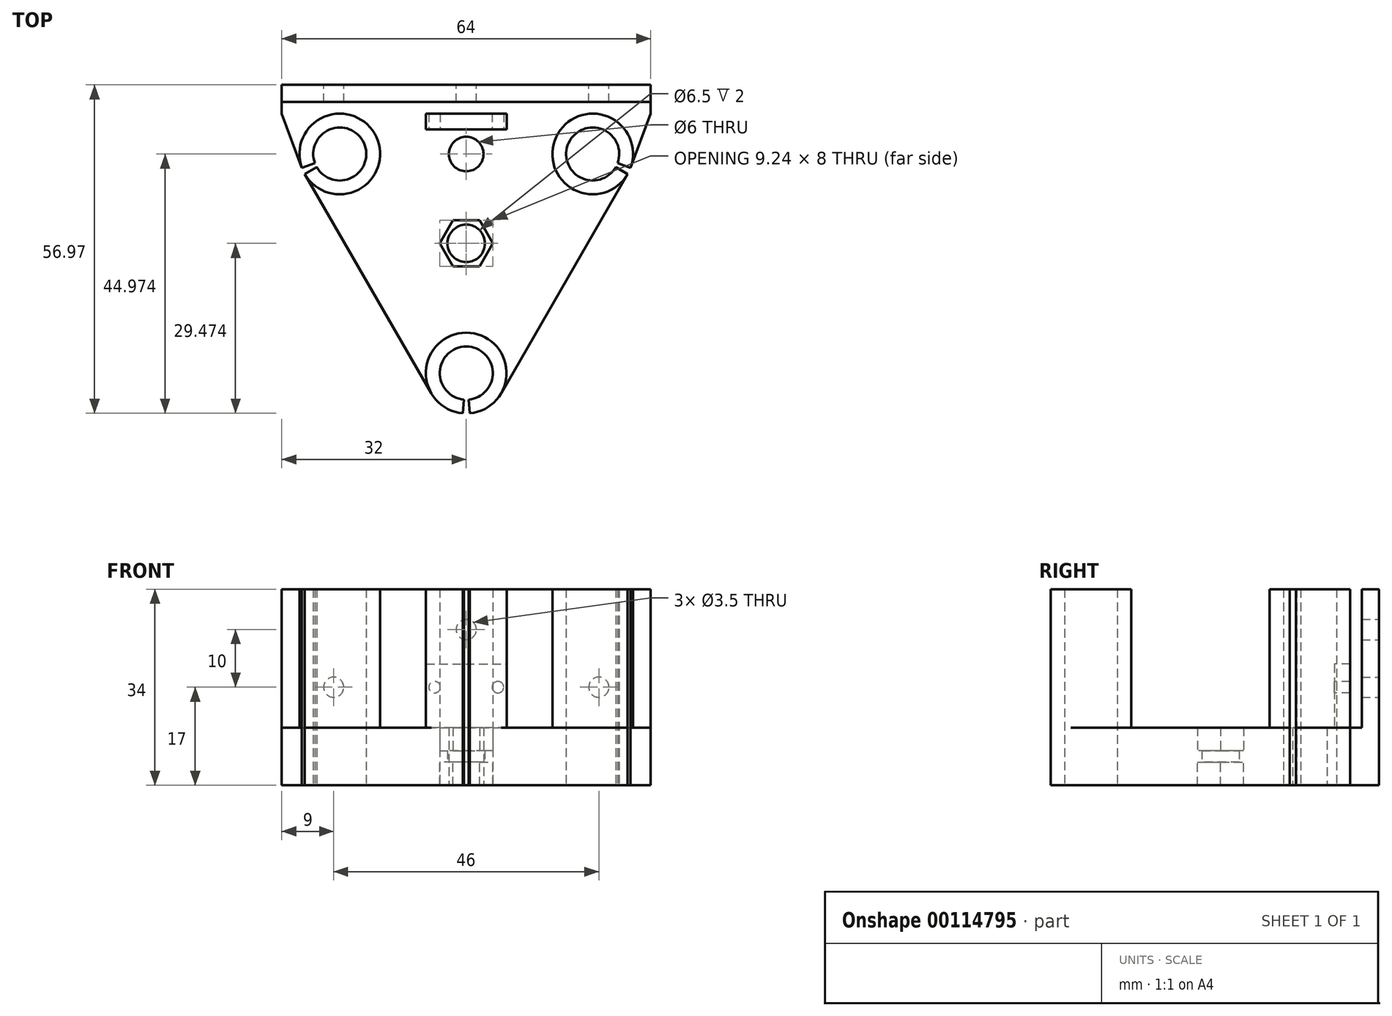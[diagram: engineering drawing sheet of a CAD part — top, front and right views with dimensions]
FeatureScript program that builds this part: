
annotation { "Feature Type Name" : "Feature", "Feature Type Description" : "" }
export const myFeature = defineFeature(function(context is Context, id is Id, definition is map)
    precondition{}
    {
        {
            var Q0;
            Q0=qCreatedBy(makeId("Top.planeOp"),FACE);
            var sketch = newSketch(context, id + "F0", { "sketchPlane" : qUnion([Q0])});
            skLineSegment(sketch, "E0", {"start": v(0, -40.44) * mm, "end": v(0, -2.44) * mm});
            skLineSegment(sketch, "E1", {"start": v(0, -40.44) * mm, "end": v(-21.94, -2.44) * mm});
            skCircle(sketch, "E2", {"center": v(-21.94, -2.44) * mm, "radius": 4.6 * mm});
            skCircle(sketch, "E3", {"center": v(-21.94, -2.44) * mm, "radius": 7 * mm});
            skCircle(sketch, "E4", {"center": v(0, -40.44) * mm, "radius": 7 * mm});
            skCircle(sketch, "E5", {"center": v(0, -40.44) * mm, "radius": 4.6 * mm});
            skLineSegment(sketch, "E6", {"start": v(0, -2.44) * mm, "end": v(0, -33.44) * mm});
            skPoint(sketch, "E7", {"position": v(0, -17.94) * mm});
            skLineSegment(sketch, "E8", {"start": v(0, -40.44) * mm, "end": v(-6.06, -43.94) * mm});
            skLineSegment(sketch, "E9", {"start": v(-21.94, -2.44) * mm, "end": v(-28, -5.94) * mm});
            skLineSegment(sketch, "E10.left", {"start": v(0, -40.44) * mm, "end": v(0, 9.56) * mm});
            skLineSegment(sketch, "E11", {"start": v(0, -40.44) * mm, "end": v(-1.01, -47.36) * mm});
            skLineSegment(sketch, "E12", {"start": v(0, -40.44) * mm, "end": v(0.61, -47.4) * mm});
            skLineSegment(sketch, "E13", {"start": v(-21.94, -2.44) * mm, "end": v(-28.52, -4.83) * mm});
            skCircle(sketch, "E14", {"center": v(0, -2.44) * mm, "radius": 3 * mm});
            skLineSegment(sketch, "E15", {"start": v(-21.94, -2.44) * mm, "end": v(-25.44, 3.63) * mm});
            skCircle(sketch, "E16.cCircle", {"center": v(0, -17.94) * mm, "radius": 4 * mm, "construction": true});
            skLineSegment(sketch, "E16.0", {"start": v(-2.3, -13.94) * mm, "end": v(2.3, -13.94) * mm});
            skLineSegment(sketch, "E16.1", {"start": v(2.3, -13.94) * mm, "end": v(4.62, -17.94) * mm});
            skLineSegment(sketch, "E16.2", {"start": v(4.62, -17.94) * mm, "end": v(2.3, -21.94) * mm});
            skLineSegment(sketch, "E16.3", {"start": v(2.3, -21.94) * mm, "end": v(-2.3, -21.94) * mm});
            skLineSegment(sketch, "E16.4", {"start": v(-2.3, -21.94) * mm, "end": v(-4.62, -17.94) * mm});
            skLineSegment(sketch, "E16.5", {"start": v(-4.62, -17.94) * mm, "end": v(-2.3, -13.94) * mm});
            skPoint(sketch, "E16.0.midPoint", {"position": v(0, -13.94) * mm});
            skCircle(sketch, "E17", {"center": v(0, -17.94) * mm, "radius": 3.25 * mm});
            skLineSegment(sketch, "E18", {"start": v(-32, 4.56) * mm, "end": v(-32, 9.56) * mm});
            skLineSegment(sketch, "E19", {"start": v(-32, 9.56) * mm, "end": v(0, 9.56) * mm});
            skLineSegment(sketch, "E20", {"start": v(0, 6.56) * mm, "end": v(-32, 6.56) * mm});
            skLineSegment(sketch, "E21", {"start": v(0, 4.56) * mm, "end": v(-7, 4.56) * mm});
            skLineSegment(sketch, "E22", {"start": v(-7, 4.56) * mm, "end": v(-7, 1.83) * mm});
            skLineSegment(sketch, "E23", {"start": v(-7, 1.83) * mm, "end": v(0, 1.83) * mm});
            skLineSegment(sketch, "E24", {"start": v(-6.06, -43.94) * mm, "end": v(-28, -5.94) * mm});
            skLineSegment(sketch, "E25", {"start": v(-32, 4.56) * mm, "end": v(-28.52, -4.83) * mm});
            skSolve(sketch);
        }
        {
            var Q0;
            {var subQ20=sQuery(id+"F0.wireOp",EDGE,"E16.4");Q0=makeQuery(id+"F0.imprint","IMPRINT",FACE,{"disambiguationData":[TD([[makeQuery(id+"F0.imprint","IMPRINT",EDGE,{"derivedFrom":subQ20}),1.0]])]});}
            var Q1;
            {var subQ5=sQuery(id+"F0.wireOp",EDGE,"E24");Q1=makeQuery(id+"F0.imprint","IMPRINT",FACE,{"disambiguationData":[TD([[makeQuery(id+"F0.imprint","IMPRINT",EDGE,{"derivedFrom":subQ5}),-1.0]])]});}
            var Q2;
            {var subQ0=sQuery(id+"F0.wireOp",EDGE,"E3");var subQ1=sQuery(id+"F0.wireOp",EDGE,"E1");var subQ2=makeQuery(id+"F0.imprint","INTERSECT",VERTEX,{"derivedFrom":[subQ1,subQ0]});Q2=makeQuery(id+"F0.imprint","IMPRINT",FACE,{"disambiguationData":[TD([[makeQuery(id+"F0.imprint","IMPRINT",EDGE,{"disambiguationData":[TD([[subQ2,-1.0]])],"derivedFrom":subQ1}),-1.0]])]});}
            var Q3;
            {var subQ0=sQuery(id+"F0.wireOp",EDGE,"E3");var subQ1=sQuery(id+"F0.wireOp",EDGE,"E1");var subQ2=makeQuery(id+"F0.imprint","INTERSECT",VERTEX,{"derivedFrom":[subQ1,subQ0]});Q3=makeQuery(id+"F0.imprint","IMPRINT",FACE,{"disambiguationData":[TD([[makeQuery(id+"F0.imprint","IMPRINT",EDGE,{"disambiguationData":[TD([[subQ2,-1.0]])],"derivedFrom":subQ1}),1.0]])]});}
            var Q4;
            {var subQ0=sQuery(id+"F0.wireOp",EDGE,"E13");var subQ1=sQuery(id+"F0.wireOp",EDGE,"E2");var subQ2=makeQuery(id+"F0.imprint","INTERSECT",VERTEX,{"derivedFrom":[subQ1,subQ0]});Q4=makeQuery(id+"F0.imprint","IMPRINT",FACE,{"disambiguationData":[TD([[makeQuery(id+"F0.imprint","IMPRINT",EDGE,{"disambiguationData":[TD([[subQ2,1.0]])],"derivedFrom":subQ1}),-1.0]])]});}
            var Q5;
            {var subQ0=sQuery(id+"F0.wireOp",EDGE,"E19");Q5=makeQuery(id+"F0.imprint","IMPRINT",FACE,{"disambiguationData":[TD([[makeQuery(id+"F0.imprint","IMPRINT",EDGE,{"derivedFrom":subQ0}),-1.0]])]});}
            var Q6;
            {var subQ0=sQuery(id+"F0.wireOp",EDGE,"E21");Q6=makeQuery(id+"F0.imprint","IMPRINT",FACE,{"disambiguationData":[TD([[makeQuery(id+"F0.imprint","IMPRINT",EDGE,{"derivedFrom":subQ0}),1.0]])]});}
            var Q7;
            {var subQ0=sQuery(id+"F0.wireOp",EDGE,"E5");var subQ1=sQuery(id+"F0.wireOp",EDGE,"E1");var subQ2=makeQuery(id+"F0.imprint","INTERSECT",VERTEX,{"derivedFrom":[subQ1,subQ0]});Q7=makeQuery(id+"F0.imprint","IMPRINT",FACE,{"disambiguationData":[TD([[makeQuery(id+"F0.imprint","IMPRINT",EDGE,{"disambiguationData":[TD([[subQ2,-1.0]])],"derivedFrom":subQ1}),-1.0]])]});}
            var Q8;
            {var subQ0=sQuery(id+"F0.wireOp",EDGE,"E12");var subQ1=sQuery(id+"F0.wireOp",EDGE,"E4");var subQ2=makeQuery(id+"F0.imprint","INTERSECT",VERTEX,{"derivedFrom":[subQ1,subQ0]});Q8=makeQuery(id+"F0.imprint","IMPRINT",FACE,{"disambiguationData":[TD([[makeQuery(id+"F0.imprint","IMPRINT",EDGE,{"disambiguationData":[TD([[subQ2,-1.0]])],"derivedFrom":subQ1}),1.0]])]});}
            var Q9;
            {var subQ0=sQuery(id+"F0.wireOp",EDGE,"E5");var subQ1=sQuery(id+"F0.wireOp",EDGE,"E1");var subQ2=makeQuery(id+"F0.imprint","INTERSECT",VERTEX,{"derivedFrom":[subQ1,subQ0]});Q9=makeQuery(id+"F0.imprint","IMPRINT",FACE,{"disambiguationData":[TD([[makeQuery(id+"F0.imprint","IMPRINT",EDGE,{"disambiguationData":[TD([[subQ2,-1.0]])],"derivedFrom":subQ1}),1.0]])]});}
            var Q10;
            {var subQ0=sQuery(id+"F0.wireOp",EDGE,"E8");var subQ5=sQuery(id+"F0.wireOp",EDGE,"E5");var subQ6=makeQuery(id+"F0.imprint","INTERSECT",VERTEX,{"derivedFrom":[subQ5,subQ0]});Q10=makeQuery(id+"F0.imprint","IMPRINT",FACE,{"disambiguationData":[TD([[makeQuery(id+"F0.imprint","IMPRINT",EDGE,{"disambiguationData":[TD([[subQ6,-1.0]])],"derivedFrom":subQ5}),-1.0]])]});}
            var Q11;
            {var subQ4=sQuery(id+"F0.wireOp",EDGE,"E16.4");Q11=makeQuery(id+"F0.imprint","IMPRINT",FACE,{"disambiguationData":[TD([[makeQuery(id+"F0.imprint","IMPRINT",EDGE,{"derivedFrom":subQ4}),-1.0]])]});}
            extrude(context, id + "F1", {"entities" : qUnion([Q0, Q1, Q2, Q3, Q4, Q5, Q6, Q7, Q8, Q9, Q10, Q11]), "depth" : 2 * mm});
        }
        {
            var Q0;
            {var subQ5=sQuery(id+"F0.wireOp",EDGE,"E24");Q0=makeQuery(id+"F0.imprint","IMPRINT",FACE,{"disambiguationData":[TD([[makeQuery(id+"F0.imprint","IMPRINT",EDGE,{"derivedFrom":subQ5}),-1.0]])]});}
            var Q1;
            {var subQ0=sQuery(id+"F0.wireOp",EDGE,"E5");var subQ1=sQuery(id+"F0.wireOp",EDGE,"E1");var subQ2=makeQuery(id+"F0.imprint","INTERSECT",VERTEX,{"derivedFrom":[subQ1,subQ0]});Q1=makeQuery(id+"F0.imprint","IMPRINT",FACE,{"disambiguationData":[TD([[makeQuery(id+"F0.imprint","IMPRINT",EDGE,{"disambiguationData":[TD([[subQ2,-1.0]])],"derivedFrom":subQ1}),1.0]])]});}
            var Q2;
            {var subQ0=sQuery(id+"F0.wireOp",EDGE,"E8");var subQ5=sQuery(id+"F0.wireOp",EDGE,"E5");var subQ6=makeQuery(id+"F0.imprint","INTERSECT",VERTEX,{"derivedFrom":[subQ5,subQ0]});Q2=makeQuery(id+"F0.imprint","IMPRINT",FACE,{"disambiguationData":[TD([[makeQuery(id+"F0.imprint","IMPRINT",EDGE,{"disambiguationData":[TD([[subQ6,-1.0]])],"derivedFrom":subQ5}),-1.0]])]});}
            var Q3;
            {var subQ0=sQuery(id+"F0.wireOp",EDGE,"E12");var subQ1=sQuery(id+"F0.wireOp",EDGE,"E4");var subQ2=makeQuery(id+"F0.imprint","INTERSECT",VERTEX,{"derivedFrom":[subQ1,subQ0]});Q3=makeQuery(id+"F0.imprint","IMPRINT",FACE,{"disambiguationData":[TD([[makeQuery(id+"F0.imprint","IMPRINT",EDGE,{"disambiguationData":[TD([[subQ2,-1.0]])],"derivedFrom":subQ1}),1.0]])]});}
            var Q4;
            {var subQ0=sQuery(id+"F0.wireOp",EDGE,"E5");var subQ1=sQuery(id+"F0.wireOp",EDGE,"E1");var subQ2=makeQuery(id+"F0.imprint","INTERSECT",VERTEX,{"derivedFrom":[subQ1,subQ0]});Q4=makeQuery(id+"F0.imprint","IMPRINT",FACE,{"disambiguationData":[TD([[makeQuery(id+"F0.imprint","IMPRINT",EDGE,{"disambiguationData":[TD([[subQ2,-1.0]])],"derivedFrom":subQ1}),-1.0]])]});}
            var Q5;
            {var subQ20=sQuery(id+"F0.wireOp",EDGE,"E16.4");Q5=makeQuery(id+"F0.imprint","IMPRINT",FACE,{"disambiguationData":[TD([[makeQuery(id+"F0.imprint","IMPRINT",EDGE,{"derivedFrom":subQ20}),1.0]])]});}
            var Q6;
            {var subQ0=sQuery(id+"F0.wireOp",EDGE,"E3");var subQ1=sQuery(id+"F0.wireOp",EDGE,"E1");var subQ2=makeQuery(id+"F0.imprint","INTERSECT",VERTEX,{"derivedFrom":[subQ1,subQ0]});Q6=makeQuery(id+"F0.imprint","IMPRINT",FACE,{"disambiguationData":[TD([[makeQuery(id+"F0.imprint","IMPRINT",EDGE,{"disambiguationData":[TD([[subQ2,-1.0]])],"derivedFrom":subQ1}),-1.0]])]});}
            var Q7;
            {var subQ0=sQuery(id+"F0.wireOp",EDGE,"E3");var subQ1=sQuery(id+"F0.wireOp",EDGE,"E1");var subQ2=makeQuery(id+"F0.imprint","INTERSECT",VERTEX,{"derivedFrom":[subQ1,subQ0]});Q7=makeQuery(id+"F0.imprint","IMPRINT",FACE,{"disambiguationData":[TD([[makeQuery(id+"F0.imprint","IMPRINT",EDGE,{"disambiguationData":[TD([[subQ2,-1.0]])],"derivedFrom":subQ1}),1.0]])]});}
            var Q8;
            {var subQ0=sQuery(id+"F0.wireOp",EDGE,"E13");var subQ1=sQuery(id+"F0.wireOp",EDGE,"E2");var subQ2=makeQuery(id+"F0.imprint","INTERSECT",VERTEX,{"derivedFrom":[subQ1,subQ0]});Q8=makeQuery(id+"F0.imprint","IMPRINT",FACE,{"disambiguationData":[TD([[makeQuery(id+"F0.imprint","IMPRINT",EDGE,{"disambiguationData":[TD([[subQ2,1.0]])],"derivedFrom":subQ1}),-1.0]])]});}
            var Q9;
            {var subQ0=sQuery(id+"F0.wireOp",EDGE,"E19");Q9=makeQuery(id+"F0.imprint","IMPRINT",FACE,{"disambiguationData":[TD([[makeQuery(id+"F0.imprint","IMPRINT",EDGE,{"derivedFrom":subQ0}),-1.0]])]});}
            var Q10;
            {var subQ0=sQuery(id+"F0.wireOp",EDGE,"E21");Q10=makeQuery(id+"F0.imprint","IMPRINT",FACE,{"disambiguationData":[TD([[makeQuery(id+"F0.imprint","IMPRINT",EDGE,{"derivedFrom":subQ0}),1.0]])]});}
            extrude(context, id + "F2", {"entities" : qUnion([Q0, Q1, Q2, Q3, Q4, Q5, Q6, Q7, Q8, Q9, Q10]), "operationType" : NewBodyOperationType.ADD, "depth" : 6 * mm});
        }
        {
            var Q0;
            {var subQ0=sQuery(id+"F0.wireOp",EDGE,"E12");var subQ1=sQuery(id+"F0.wireOp",EDGE,"E4");var subQ2=makeQuery(id+"F0.imprint","INTERSECT",VERTEX,{"derivedFrom":[subQ1,subQ0]});Q0=makeQuery(id+"F0.imprint","IMPRINT",FACE,{"disambiguationData":[TD([[makeQuery(id+"F0.imprint","IMPRINT",EDGE,{"disambiguationData":[TD([[subQ2,-1.0]])],"derivedFrom":subQ1}),1.0]])]});}
            var Q1;
            {var subQ0=sQuery(id+"F0.wireOp",EDGE,"E5");var subQ1=sQuery(id+"F0.wireOp",EDGE,"E1");var subQ2=makeQuery(id+"F0.imprint","INTERSECT",VERTEX,{"derivedFrom":[subQ1,subQ0]});Q1=makeQuery(id+"F0.imprint","IMPRINT",FACE,{"disambiguationData":[TD([[makeQuery(id+"F0.imprint","IMPRINT",EDGE,{"disambiguationData":[TD([[subQ2,-1.0]])],"derivedFrom":subQ1}),-1.0]])]});}
            var Q2;
            {var subQ0=sQuery(id+"F0.wireOp",EDGE,"E5");var subQ1=sQuery(id+"F0.wireOp",EDGE,"E1");var subQ2=makeQuery(id+"F0.imprint","INTERSECT",VERTEX,{"derivedFrom":[subQ1,subQ0]});Q2=makeQuery(id+"F0.imprint","IMPRINT",FACE,{"disambiguationData":[TD([[makeQuery(id+"F0.imprint","IMPRINT",EDGE,{"disambiguationData":[TD([[subQ2,-1.0]])],"derivedFrom":subQ1}),1.0]])]});}
            var Q3;
            {var subQ0=sQuery(id+"F0.wireOp",EDGE,"E8");var subQ5=sQuery(id+"F0.wireOp",EDGE,"E5");var subQ6=makeQuery(id+"F0.imprint","INTERSECT",VERTEX,{"derivedFrom":[subQ5,subQ0]});Q3=makeQuery(id+"F0.imprint","IMPRINT",FACE,{"disambiguationData":[TD([[makeQuery(id+"F0.imprint","IMPRINT",EDGE,{"disambiguationData":[TD([[subQ6,-1.0]])],"derivedFrom":subQ5}),-1.0]])]});}
            var Q4;
            {var subQ0=sQuery(id+"F0.wireOp",EDGE,"E3");var subQ1=sQuery(id+"F0.wireOp",EDGE,"E1");var subQ2=makeQuery(id+"F0.imprint","INTERSECT",VERTEX,{"derivedFrom":[subQ1,subQ0]});Q4=makeQuery(id+"F0.imprint","IMPRINT",FACE,{"disambiguationData":[TD([[makeQuery(id+"F0.imprint","IMPRINT",EDGE,{"disambiguationData":[TD([[subQ2,-1.0]])],"derivedFrom":subQ1}),1.0]])]});}
            var Q5;
            {var subQ0=sQuery(id+"F0.wireOp",EDGE,"E3");var subQ1=sQuery(id+"F0.wireOp",EDGE,"E1");var subQ2=makeQuery(id+"F0.imprint","INTERSECT",VERTEX,{"derivedFrom":[subQ1,subQ0]});Q5=makeQuery(id+"F0.imprint","IMPRINT",FACE,{"disambiguationData":[TD([[makeQuery(id+"F0.imprint","IMPRINT",EDGE,{"disambiguationData":[TD([[subQ2,-1.0]])],"derivedFrom":subQ1}),-1.0]])]});}
            var Q6;
            {var subQ0=sQuery(id+"F0.wireOp",EDGE,"E13");var subQ1=sQuery(id+"F0.wireOp",EDGE,"E2");var subQ2=makeQuery(id+"F0.imprint","INTERSECT",VERTEX,{"derivedFrom":[subQ1,subQ0]});Q6=makeQuery(id+"F0.imprint","IMPRINT",FACE,{"disambiguationData":[TD([[makeQuery(id+"F0.imprint","IMPRINT",EDGE,{"disambiguationData":[TD([[subQ2,1.0]])],"derivedFrom":subQ1}),-1.0]])]});}
            var Q7;
            {var subQ0=sQuery(id+"F0.wireOp",EDGE,"E19");Q7=makeQuery(id+"F0.imprint","IMPRINT",FACE,{"disambiguationData":[TD([[makeQuery(id+"F0.imprint","IMPRINT",EDGE,{"derivedFrom":subQ0}),-1.0]])]});}
            extrude(context, id + "F3", {"entities" : qUnion([Q0, Q1, Q2, Q3, Q4, Q5, Q6, Q7]), "operationType" : NewBodyOperationType.ADD, "depth" : 30 * mm});
        }
        {
            var Q0;
            {var subQ0=sQuery(id+"F0.wireOp",EDGE,"E21");Q0=makeQuery(id+"F0.imprint","IMPRINT",FACE,{"disambiguationData":[TD([[makeQuery(id+"F0.imprint","IMPRINT",EDGE,{"derivedFrom":subQ0}),1.0]])]});}
            extrude(context, id + "F4", {"entities" : qUnion([Q0]), "operationType" : NewBodyOperationType.ADD, "depth" : 20 * mm});
        }
        {
            var Q0;
            {var subQ5=sQuery(id+"F0.wireOp",EDGE,"E24");Q0=makeQuery(id+"F0.imprint","IMPRINT",FACE,{"disambiguationData":[TD([[makeQuery(id+"F0.imprint","IMPRINT",EDGE,{"derivedFrom":subQ5}),-1.0]])]});}
            var Q1;
            {var subQ0=sQuery(id+"F0.wireOp",EDGE,"E8");var subQ5=sQuery(id+"F0.wireOp",EDGE,"E5");var subQ6=makeQuery(id+"F0.imprint","INTERSECT",VERTEX,{"derivedFrom":[subQ5,subQ0]});Q1=makeQuery(id+"F0.imprint","IMPRINT",FACE,{"disambiguationData":[TD([[makeQuery(id+"F0.imprint","IMPRINT",EDGE,{"disambiguationData":[TD([[subQ6,-1.0]])],"derivedFrom":subQ5}),-1.0]])]});}
            var Q2;
            {var subQ0=sQuery(id+"F0.wireOp",EDGE,"E5");var subQ1=sQuery(id+"F0.wireOp",EDGE,"E1");var subQ2=makeQuery(id+"F0.imprint","INTERSECT",VERTEX,{"derivedFrom":[subQ1,subQ0]});Q2=makeQuery(id+"F0.imprint","IMPRINT",FACE,{"disambiguationData":[TD([[makeQuery(id+"F0.imprint","IMPRINT",EDGE,{"disambiguationData":[TD([[subQ2,-1.0]])],"derivedFrom":subQ1}),1.0]])]});}
            var Q3;
            {var subQ0=sQuery(id+"F0.wireOp",EDGE,"E5");var subQ1=sQuery(id+"F0.wireOp",EDGE,"E1");var subQ2=makeQuery(id+"F0.imprint","INTERSECT",VERTEX,{"derivedFrom":[subQ1,subQ0]});Q3=makeQuery(id+"F0.imprint","IMPRINT",FACE,{"disambiguationData":[TD([[makeQuery(id+"F0.imprint","IMPRINT",EDGE,{"disambiguationData":[TD([[subQ2,-1.0]])],"derivedFrom":subQ1}),-1.0]])]});}
            var Q4;
            {var subQ0=sQuery(id+"F0.wireOp",EDGE,"E12");var subQ1=sQuery(id+"F0.wireOp",EDGE,"E4");var subQ2=makeQuery(id+"F0.imprint","INTERSECT",VERTEX,{"derivedFrom":[subQ1,subQ0]});Q4=makeQuery(id+"F0.imprint","IMPRINT",FACE,{"disambiguationData":[TD([[makeQuery(id+"F0.imprint","IMPRINT",EDGE,{"disambiguationData":[TD([[subQ2,-1.0]])],"derivedFrom":subQ1}),1.0]])]});}
            var Q5;
            {var subQ20=sQuery(id+"F0.wireOp",EDGE,"E16.4");Q5=makeQuery(id+"F0.imprint","IMPRINT",FACE,{"disambiguationData":[TD([[makeQuery(id+"F0.imprint","IMPRINT",EDGE,{"derivedFrom":subQ20}),1.0]])]});}
            var Q6;
            {var subQ0=sQuery(id+"F0.wireOp",EDGE,"E21");Q6=makeQuery(id+"F0.imprint","IMPRINT",FACE,{"disambiguationData":[TD([[makeQuery(id+"F0.imprint","IMPRINT",EDGE,{"derivedFrom":subQ0}),1.0]])]});}
            var Q7;
            {var subQ0=sQuery(id+"F0.wireOp",EDGE,"E19");Q7=makeQuery(id+"F0.imprint","IMPRINT",FACE,{"disambiguationData":[TD([[makeQuery(id+"F0.imprint","IMPRINT",EDGE,{"derivedFrom":subQ0}),-1.0]])]});}
            var Q8;
            {var subQ0=sQuery(id+"F0.wireOp",EDGE,"E3");var subQ1=sQuery(id+"F0.wireOp",EDGE,"E1");var subQ2=makeQuery(id+"F0.imprint","INTERSECT",VERTEX,{"derivedFrom":[subQ1,subQ0]});Q8=makeQuery(id+"F0.imprint","IMPRINT",FACE,{"disambiguationData":[TD([[makeQuery(id+"F0.imprint","IMPRINT",EDGE,{"disambiguationData":[TD([[subQ2,-1.0]])],"derivedFrom":subQ1}),-1.0]])]});}
            var Q9;
            {var subQ0=sQuery(id+"F0.wireOp",EDGE,"E3");var subQ1=sQuery(id+"F0.wireOp",EDGE,"E1");var subQ2=makeQuery(id+"F0.imprint","INTERSECT",VERTEX,{"derivedFrom":[subQ1,subQ0]});Q9=makeQuery(id+"F0.imprint","IMPRINT",FACE,{"disambiguationData":[TD([[makeQuery(id+"F0.imprint","IMPRINT",EDGE,{"disambiguationData":[TD([[subQ2,-1.0]])],"derivedFrom":subQ1}),1.0]])]});}
            var Q10;
            {var subQ0=sQuery(id+"F0.wireOp",EDGE,"E13");var subQ1=sQuery(id+"F0.wireOp",EDGE,"E2");var subQ2=makeQuery(id+"F0.imprint","INTERSECT",VERTEX,{"derivedFrom":[subQ1,subQ0]});Q10=makeQuery(id+"F0.imprint","IMPRINT",FACE,{"disambiguationData":[TD([[makeQuery(id+"F0.imprint","IMPRINT",EDGE,{"disambiguationData":[TD([[subQ2,1.0]])],"derivedFrom":subQ1}),-1.0]])]});}
            extrude(context, id + "F5", {"entities" : qUnion([Q0, Q1, Q2, Q3, Q4, Q5, Q6, Q7, Q8, Q9, Q10]), "operationType" : NewBodyOperationType.ADD, "oppositeDirection" : true, "depth" : 4 * mm});
        }
        {
            var Q0;
            Q0=makeQuery(id+"F4.opExtrude","SWEPT_FACE",FACE,{"disambiguationData":[OSD([sQuery(id+"F0.wireOp",EDGE,"E23")])]});
            var sketch = newSketch(context, id + "F6", { "sketchPlane" : qUnion([Q0])});
            skLineSegment(sketch, "E26", {"start": v(0, 13) * mm, "end": v(-5.5, 13) * mm});
            skCircle(sketch, "E27", {"center": v(-5.5, 13) * mm, "radius": 1 * mm});
            skSolve(sketch);
        }
        {
            var Q0;
            Q0=makeQuery(id+"F6.imprint","IMPRINT",FACE,{"disambiguationData":[TD([[makeQuery(id+"F6.imprint","IMPRINT",EDGE,{"derivedFrom":sQuery(id+"F6.wireOp",EDGE,"E27")}),1.0]])]});
            extrude(context, id + "F7", {"entities" : qUnion([Q0]), "operationType" : NewBodyOperationType.REMOVE, "oppositeDirection" : true, "depth" : 3 * mm});
        }
        {
            var Q0;
            {var subQ0=sQuery(id+"F0.wireOp",EDGE,"E19");Q0=makeQuery(id+"F5.boolean.opBoolean","MERGE",FACE,{"derivedFrom":[makeQuery(id+"F3.boolean.opBoolean","MERGE",FACE,{"derivedFrom":[makeQuery(id+"F2.boolean.opBoolean","MERGE",FACE,{"derivedFrom":[makeQuery(id+"F1.opExtrude","SWEPT_FACE",FACE,{"disambiguationData":[OSD([subQ0])]}),makeQuery(id+"F2.opExtrude","SWEPT_FACE",FACE,{"disambiguationData":[OSD([subQ0])]})]}),makeQuery(id+"F3.opExtrude","SWEPT_FACE",FACE,{"disambiguationData":[OSD([subQ0])]})]}),makeQuery(id+"F5.opExtrude","SWEPT_FACE",FACE,{"disambiguationData":[OSD([subQ0])]})]});}
            var sketch = newSketch(context, id + "F8", { "sketchPlane" : qUnion([Q0])});
            skLineSegment(sketch, "E28", {"start": v(0, 13) * mm, "end": v(23, 13) * mm});
            skCircle(sketch, "E29", {"center": v(23, 13) * mm, "radius": 1.75 * mm});
            skCircle(sketch, "E30", {"center": v(0, 23) * mm, "radius": 1.75 * mm});
            skLineSegment(sketch, "E31", {"start": v(0, 23) * mm, "end": v(0, 13) * mm});
            skSolve(sketch);
        }
        {
            var Q0;
            {var subQ0=sQuery(id+"F8.wireOp",EDGE,"E31");var subQ1=sQuery(id+"F8.wireOp",EDGE,"E30");var subQ2=makeQuery(id+"F8.imprint","INTERSECT",VERTEX,{"derivedFrom":[subQ1,subQ0]});Q0=makeQuery(id+"F8.imprint","IMPRINT",FACE,{"disambiguationData":[TD([[makeQuery(id+"F8.imprint","IMPRINT",EDGE,{"disambiguationData":[TD([[subQ2,-1.0]])],"derivedFrom":subQ1}),1.0]])]});}
            var Q1;
            Q1=makeQuery(id+"F8.imprint","IMPRINT",FACE,{"disambiguationData":[TD([[makeQuery(id+"F8.imprint","IMPRINT",EDGE,{"derivedFrom":sQuery(id+"F8.wireOp",EDGE,"E29")}),1.0]])]});
            extrude(context, id + "F9", {"entities" : qUnion([Q0, Q1]), "operationType" : NewBodyOperationType.REMOVE, "oppositeDirection" : true, "depth" : 3 * mm});
        }
        {
            var Q0;
            Q0=makeQuery(id+"F4.opExtrude","CAP_FACE",FACE,{"disambiguationData":[OSD([sQuery(id+"F0.wireOp",EDGE,"E10.left"),sQuery(id+"F0.wireOp",EDGE,"E21"),sQuery(id+"F0.wireOp",EDGE,"E22"),sQuery(id+"F0.wireOp",EDGE,"E23")])],"isStart":false});
            extrude(context, id + "F10", {"entities" : qUnion([Q0]), "operationType" : NewBodyOperationType.REMOVE, "oppositeDirection" : true, "depth" : 3 * mm});
        }
        {
            var Q0;
            Q0=makeQuery(id+"F1.opExtrude","SWEPT_BODY",BODY,{"disambiguationData":[OSD([sQuery(id+"F0.wireOp",EDGE,"E2"),sQuery(id+"F0.wireOp",EDGE,"E4"),sQuery(id+"F0.wireOp",EDGE,"E5"),sQuery(id+"F0.wireOp",EDGE,"E9"),sQuery(id+"F0.wireOp",EDGE,"E10.left"),sQuery(id+"F0.wireOp",EDGE,"E11"),sQuery(id+"F0.wireOp",EDGE,"E12"),sQuery(id+"F0.wireOp",EDGE,"E13"),sQuery(id+"F0.wireOp",EDGE,"E14"),sQuery(id+"F0.wireOp",EDGE,"E17"),sQuery(id+"F0.wireOp",EDGE,"E18"),sQuery(id+"F0.wireOp",EDGE,"E19"),sQuery(id+"F0.wireOp",EDGE,"E24"),sQuery(id+"F0.wireOp",EDGE,"E25")])]});
            var Q1;
            Q1=qCreatedBy(makeId("Right.planeOp"),FACE);
            mirror(context, id + "F11", {"operationType" : NewBodyOperationType.ADD, "entities" : qUnion([Q0]), "mirrorPlane" : qUnion([Q1])});
        }
    });
